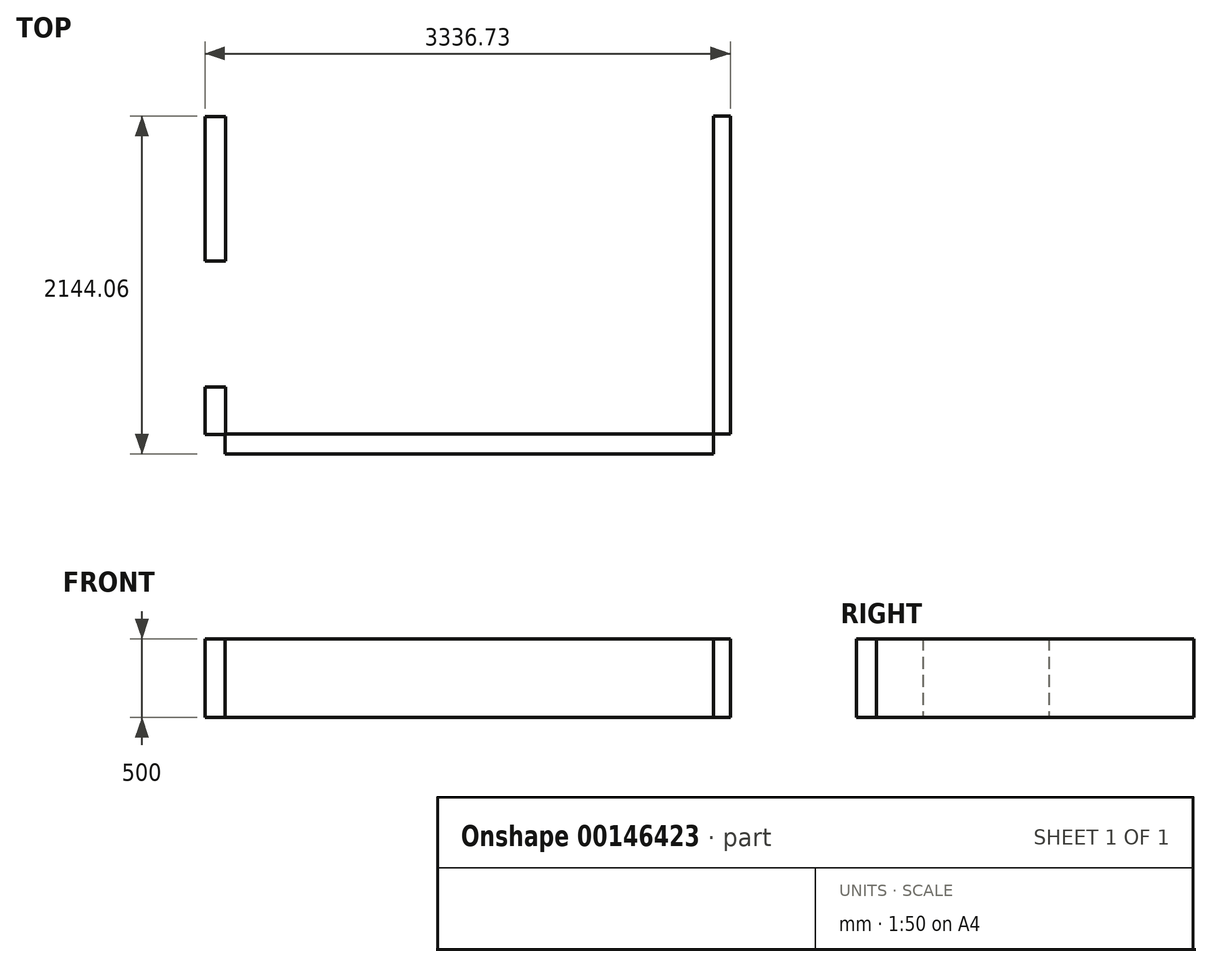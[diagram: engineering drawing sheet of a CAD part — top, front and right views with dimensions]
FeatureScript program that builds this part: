
annotation { "Feature Type Name" : "Feature", "Feature Type Description" : "" }
export const myFeature = defineFeature(function(context is Context, id is Id, definition is map)
    precondition{}
    {
        {
            var Q0;
            Q0=qCreatedBy(makeId("Top.planeOp"),FACE);
            var sketch = newSketch(context, id + "F0", { "sketchPlane" : qUnion([Q0])});
            skLineSegment(sketch, "E0.bottom", {"start": v(-3043.7, 1980.31) * mm, "end": v(56.3, 1980.31) * mm});
            skLineSegment(sketch, "E0.top", {"start": v(-3043.7, -39.69) * mm, "end": v(56.3, -39.69) * mm});
            skLineSegment(sketch, "E0.left", {"start": v(-3043.7, 1980.31) * mm, "end": v(-3043.7, -39.69) * mm});
            skLineSegment(sketch, "E0.right", {"start": v(56.3, 1980.31) * mm, "end": v(56.3, -39.69) * mm});
            skLineSegment(sketch, "E1.top", {"start": v(-3043.7, 2105) * mm, "end": v(56.3, 2105) * mm});
            skLineSegment(sketch, "E1.left", {"start": v(-3043.7, 1980.31) * mm, "end": v(-3043.7, 2105) * mm});
            skLineSegment(sketch, "E1.right", {"start": v(56.3, 1980.31) * mm, "end": v(56.3, 2105) * mm});
            skLineSegment(sketch, "E2.bottom", {"start": v(56.3, 1980.31) * mm, "end": v(162.02, 1980.31) * mm});
            skLineSegment(sketch, "E2.top", {"start": v(56.3, -36.13) * mm, "end": v(162.02, -36.13) * mm});
            skLineSegment(sketch, "E2.left", {"start": v(56.3, 1980.31) * mm, "end": v(56.3, -36.13) * mm});
            skLineSegment(sketch, "E2.right", {"start": v(162.02, 1980.31) * mm, "end": v(162.02, -36.13) * mm});
            skLineSegment(sketch, "E3.bottom", {"start": v(56.3, -36.13) * mm, "end": v(-3047.3, -36.13) * mm});
            skLineSegment(sketch, "E3.top", {"start": v(56.3, -163.75) * mm, "end": v(-3047.3, -163.75) * mm});
            skLineSegment(sketch, "E3.left", {"start": v(56.3, -36.13) * mm, "end": v(56.3, -163.75) * mm});
            skLineSegment(sketch, "E3.right", {"start": v(-3047.3, -36.13) * mm, "end": v(-3047.3, -163.75) * mm});
            skLineSegment(sketch, "E4.bottom", {"start": v(-3043.7, -39.69) * mm, "end": v(-3174.7, -39.69) * mm});
            skLineSegment(sketch, "E4.top", {"start": v(-3043.7, 1977.38) * mm, "end": v(-3174.7, 1977.38) * mm});
            skLineSegment(sketch, "E4.left", {"start": v(-3043.7, -39.69) * mm, "end": v(-3043.7, 1977.38) * mm});
            skLineSegment(sketch, "E4.right", {"start": v(-3174.7, -39.69) * mm, "end": v(-3174.7, 1977.38) * mm});
            skLineSegment(sketch, "E5.bottom", {"start": v(-3174.7, 1060.31) * mm, "end": v(-3043.7, 1060.31) * mm});
            skLineSegment(sketch, "E5.top", {"start": v(-3174.7, 260.31) * mm, "end": v(-3043.7, 260.31) * mm});
            skLineSegment(sketch, "E5.left", {"start": v(-3174.7, 1060.31) * mm, "end": v(-3174.7, 260.31) * mm});
            skLineSegment(sketch, "E5.right", {"start": v(-3043.7, 1060.31) * mm, "end": v(-3043.7, 260.31) * mm});
            skLineSegment(sketch, "E6.bottom", {"start": v(-3174.7, 260.31) * mm, "end": v(-3174.7, 260.31) * mm});
            skLineSegment(sketch, "E6.top", {"start": v(-3174.7, -39.69) * mm, "end": v(-3174.7, -39.69) * mm});
            skLineSegment(sketch, "E6.left", {"start": v(-3174.7, 260.31) * mm, "end": v(-3174.7, -39.69) * mm});
            skLineSegment(sketch, "E6.right", {"start": v(-3174.7, 260.31) * mm, "end": v(-3174.7, -39.69) * mm});
            skSolve(sketch);
        }
        {
            var Q0;
            Q0=makeQuery(id+"F0.imprint","IMPRINT",FACE,{"disambiguationData":[TD([[makeQuery(id+"F0.imprint","IMPRINT",EDGE,{"derivedFrom":sQuery(id+"F0.wireOp",EDGE,"E0.bottom")}),1.0]])]});
            var Q1;
            Q1=makeQuery(id+"F0.imprint","IMPRINT",FACE,{"disambiguationData":[TD([[makeQuery(id+"F0.imprint","IMPRINT",EDGE,{"derivedFrom":sQuery(id+"F0.wireOp",EDGE,"E2.bottom")}),-1.0]])]});
            var Q2;
            {var subQ1=sQuery(id+"F0.wireOp",EDGE,"E0.top");Q2=makeQuery(id+"F0.imprint","IMPRINT",FACE,{"disambiguationData":[TD([[makeQuery(id+"F0.imprint","IMPRINT",EDGE,{"derivedFrom":subQ1}),-1.0]])]});}
            var Q3;
            {var subQ0=sQuery(id+"F0.wireOp",EDGE,"E4.top");Q3=makeQuery(id+"F0.imprint","IMPRINT",FACE,{"disambiguationData":[TD([[makeQuery(id+"F0.imprint","IMPRINT",EDGE,{"derivedFrom":subQ0}),1.0]])]});}
            var Q4;
            {var subQ0=sQuery(id+"F0.wireOp",EDGE,"E0.top");Q4=makeQuery(id+"F0.imprint","IMPRINT",FACE,{"disambiguationData":[TD([[makeQuery(id+"F0.imprint","IMPRINT",EDGE,{"derivedFrom":subQ0}),1.0]])]});}
            var Q5;
            {var subQ0=sQuery(id+"F0.wireOp",EDGE,"E3.right");var subQ1=sQuery(id+"F0.wireOp",EDGE,"E3.bottom");var subQ2=makeQuery(id+"F0.imprint","INTERSECT",VERTEX,{"derivedFrom":[subQ1,subQ0]});Q5=makeQuery(id+"F0.imprint","IMPRINT",FACE,{"disambiguationData":[TD([[makeQuery(id+"F0.imprint","IMPRINT",EDGE,{"disambiguationData":[TD([[subQ2,1.0]])],"derivedFrom":subQ1}),1.0]])]});}
            var Q6;
            {var subQ0=sQuery(id+"F0.wireOp",EDGE,"E5.top");Q6=makeQuery(id+"F0.imprint","IMPRINT",FACE,{"disambiguationData":[TD([[makeQuery(id+"F0.imprint","IMPRINT",EDGE,{"derivedFrom":subQ0}),-1.0]])]});}
            extrude(context, id + "F1", {"entities" : qUnion([Q0, Q1, Q2, Q3, Q4, Q5, Q6]), "depth" : 500 * mm});
        }
    });
